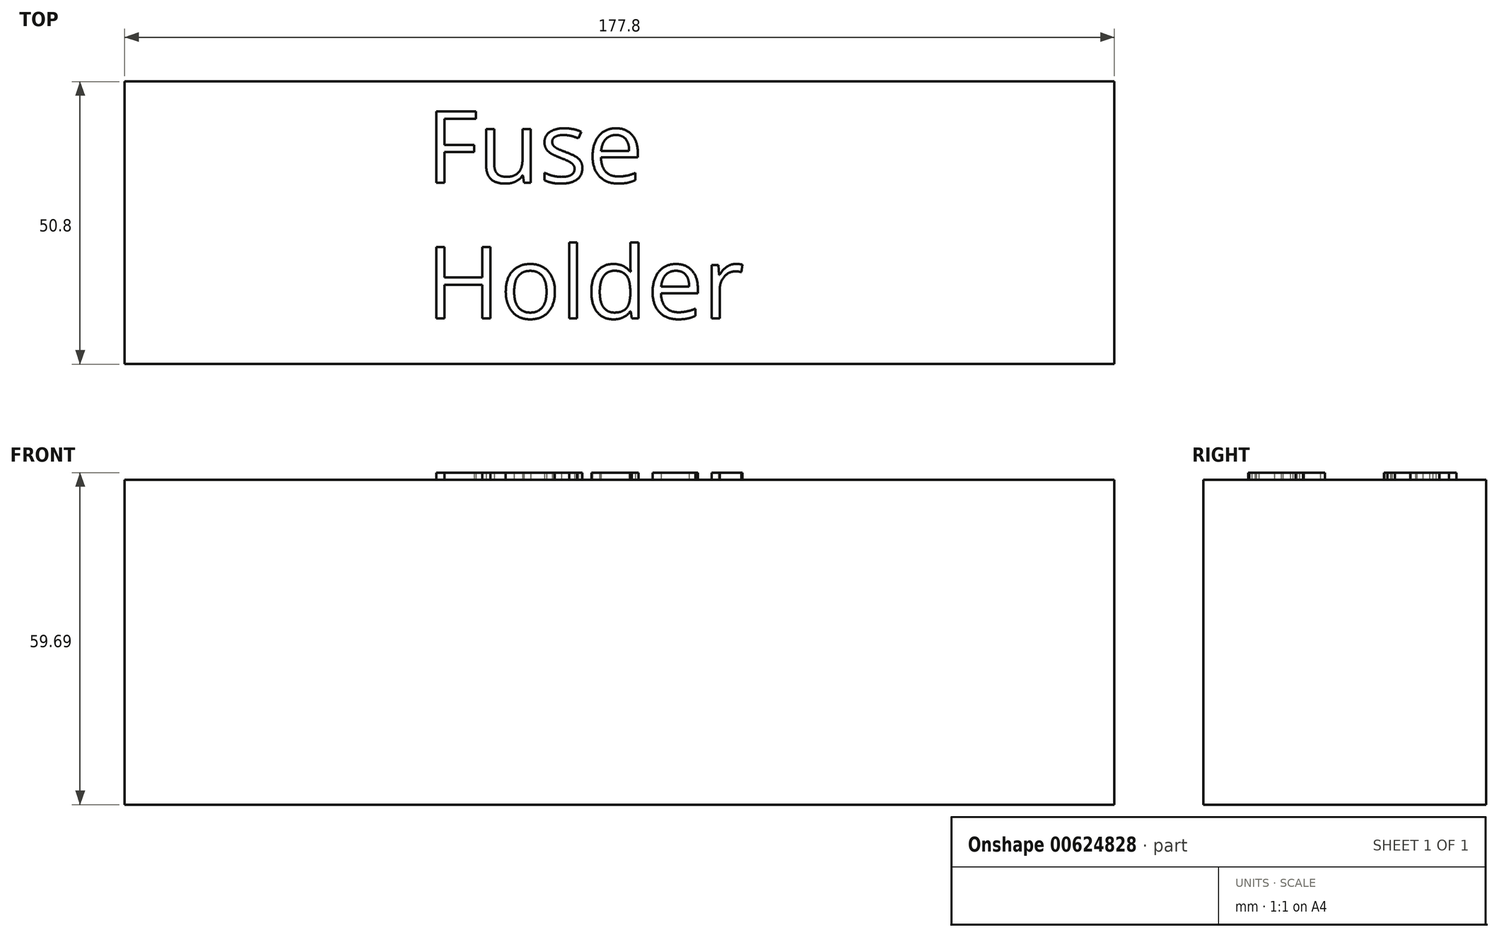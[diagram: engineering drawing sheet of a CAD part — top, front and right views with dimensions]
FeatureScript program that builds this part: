
annotation { "Feature Type Name" : "Feature", "Feature Type Description" : "" }
export const myFeature = defineFeature(function(context is Context, id is Id, definition is map)
    precondition{}
    {
        {
            var Q0;
            Q0=qCreatedBy(makeId("Top.planeOp"),FACE);
            var sketch = newSketch(context, id + "F0", { "sketchPlane" : qUnion([Q0])});
            skLineSegment(sketch, "E0.bottom", {"start": v(-100.26, 22.45) * mm, "end": v(77.54, 22.45) * mm});
            skLineSegment(sketch, "E0.top", {"start": v(-100.26, -28.35) * mm, "end": v(77.54, -28.35) * mm});
            skLineSegment(sketch, "E0.left", {"start": v(-100.26, 22.45) * mm, "end": v(-100.26, -28.35) * mm});
            skLineSegment(sketch, "E0.right", {"start": v(77.54, 22.45) * mm, "end": v(77.54, -28.35) * mm});
            skSolve(sketch);
        }
        {
            var Q0;
            Q0=makeQuery(id+"F0.imprint","IMPRINT",FACE,{"disambiguationData":[TD([[makeQuery(id+"F0.imprint","IMPRINT",EDGE,{"derivedFrom":sQuery(id+"F0.wireOp",EDGE,"E0.bottom")}),-1.0]])]});
            extrude(context, id + "F1", {"entities" : qUnion([Q0]), "depth" : 58.42 * mm, "offsetDistance" : 25.4 * mm});
        }
        {
            var Q0;
            Q0=makeQuery(id+"F1.opExtrude","CAP_FACE",FACE,{"disambiguationData":[OSD([sQuery(id+"F0.wireOp",EDGE,"E0.bottom"),sQuery(id+"F0.wireOp",EDGE,"E0.top"),sQuery(id+"F0.wireOp",EDGE,"E0.left"),sQuery(id+"F0.wireOp",EDGE,"E0.right")])],"isStart":false});
            var sketch = newSketch(context, id + "F2", { "sketchPlane" : qUnion([Q0])});
            skText(sketch, "E1", { "text": "Fuse\nHolder", "fontName": "OpenSans-Regular.ttf"});
            const initialGuessF2  = {"E1": [-0.04604, 0.00428, 1, 0, 0.01292]};
            skSetInitialGuess(sketch, initialGuessF2);
            skSolve(sketch);
        }
        {
            var Q0;
            Q0 = qSketchRegion(id + "F2", true);
            extrude(context, id + "F3", {"entities" : qUnion([Q0]), "operationType" : NewBodyOperationType.ADD, "depth" : 1.27 * mm, "offsetDistance" : 25.4 * mm});
        }
    });
